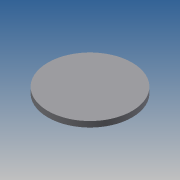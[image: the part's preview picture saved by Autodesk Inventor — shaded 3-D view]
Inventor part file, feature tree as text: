
AUTODESK INVENTOR PART (.ipt)
format: ipt  version: 2013 (Build 170138000, 138)  size: 65,536 bytes
history: native  units: mm
features: extrude x1, sketch x1
ambient origin geometry x8: Origin, YZ Plane, XZ Plane, XY Plane, X Axis, Y Axis, Z Axis, Center Point
bodies: Solid1 (feature_tree)
feature tree (2):
  extrude  "Extrusion1"  Depth=10.0mm TaperAngle=0.0deg
  sketch  "Sketch1"  dims[d0=150.0mm d2=10.0mm d3=0.0mm]
